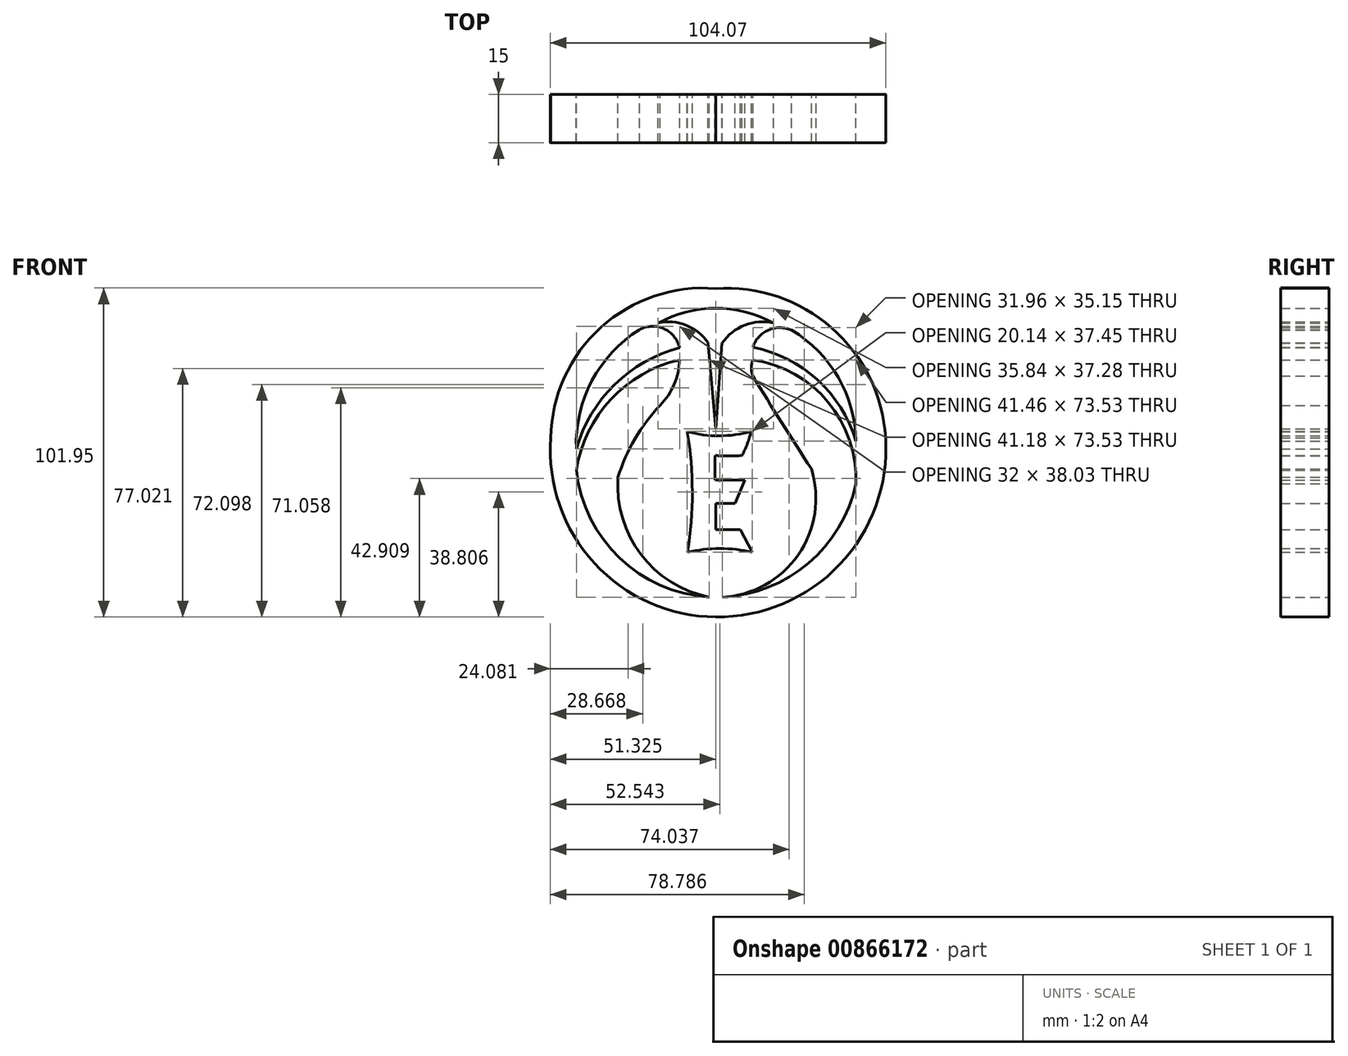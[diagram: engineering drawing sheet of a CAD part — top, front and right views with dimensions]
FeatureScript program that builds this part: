
annotation { "Feature Type Name" : "Feature", "Feature Type Description" : "" }
export const myFeature = defineFeature(function(context is Context, id is Id, definition is map)
    precondition{}
    {
        {
            var Q0;
            Q0=qCreatedBy(makeId("Front.planeOp"),FACE);
            var sketch = newSketch(context, id + "F0", { "sketchPlane" : qUnion([Q0])});
            skArc(sketch, "E0", {"start": v(0, 46.3) * mm, "mid": v(-35.58, 34.22) * mm, "end": v(-51.11, 0) * mm});
            skPoint(sketch, "E0.startSnap0", {"position": v(3.57, 46.3) * mm});
            skArc(sketch, "E1", {"start": v(-51.11, 0) * mm, "mid": v(-37.6, -38.84) * mm, "end": v(0, -55.5) * mm});
            skArc(sketch, "E2", {"start": v(0, -55.5) * mm, "mid": v(38.46, -39.25) * mm, "end": v(52.7, 0) * mm});
            skArc(sketch, "E3", {"start": v(52.7, 0) * mm, "mid": v(35.98, 34.1) * mm, "end": v(0, 46.3) * mm});
            skArc(sketch, "E4", {"start": v(-23.6, 33.52) * mm, "mid": v(-38.38, 17.67) * mm, "end": v(-43.18, -3.45) * mm});
            skArc(sketch, "E5", {"start": v(-11.18, 27.93) * mm, "mid": v(-31.35, 16.5) * mm, "end": v(-43.18, -3.45) * mm});
            skArc(sketch, "E6", {"start": v(-11.18, 27.93) * mm, "mid": v(-16, 33.83) * mm, "end": v(-23.6, 33.52) * mm});
            skArc(sketch, "E7", {"start": v(-11.18, 24.17) * mm, "mid": v(-32.46, 12) * mm, "end": v(-43.18, -10.06) * mm});
            skArc(sketch, "E8", {"start": v(-43.18, -10.06) * mm, "mid": v(-29.76, -37.21) * mm, "end": v(-2, -49.35) * mm});
            skArc(sketch, "E9", {"start": v(-30.26, -12.15) * mm, "mid": v(-23.15, -36.08) * mm, "end": v(-2, -49.35) * mm});
            skArc(sketch, "E10", {"start": v(-17.2, 10.07) * mm, "mid": v(-25, -0.3) * mm, "end": v(-30.26, -12.15) * mm});
            skArc(sketch, "E11", {"start": v(-17.2, 10.07) * mm, "mid": v(-12.89, 16.56) * mm, "end": v(-11.18, 24.17) * mm});
            skArc(sketch, "E12", {"start": v(43.5, -0.98) * mm, "mid": v(31.57, 18) * mm, "end": v(11.54, 28.12) * mm});
            skArc(sketch, "E13", {"start": v(43.5, -0.98) * mm, "mid": v(38, 18.8) * mm, "end": v(23.55, 33.39) * mm});
            skArc(sketch, "E14", {"start": v(23.55, 33.39) * mm, "mid": v(16.37, 33.43) * mm, "end": v(11.54, 28.12) * mm});
            skArc(sketch, "E15", {"start": v(43.5, -14.26) * mm, "mid": v(34.9, 11.09) * mm, "end": v(11.54, 24.17) * mm});
            skArc(sketch, "E16", {"start": v(2.05, -49.35) * mm, "mid": v(28.73, -38.84) * mm, "end": v(43.5, -14.26) * mm});
            skArc(sketch, "E17", {"start": v(2.05, -49.35) * mm, "mid": v(25.61, -36.24) * mm, "end": v(29.71, -9.58) * mm});
            skArc(sketch, "E18", {"start": v(11.54, 19.16) * mm, "mid": v(20.5, 4.72) * mm, "end": v(29.71, -9.58) * mm});
            skArc(sketch, "E19", {"start": v(11.54, 24.17) * mm, "mid": v(11.04, 21.67) * mm, "end": v(11.54, 19.16) * mm});
            skArc(sketch, "E20", {"start": v(-8.79, 1.94) * mm, "mid": v(1.13, 0.63) * mm, "end": v(11.04, 2.03) * mm});
            skPoint(sketch, "E20.endSnap0", {"position": v(11.04, 21.67) * mm});
            skArc(sketch, "E21", {"start": v(8.21, -5.45) * mm, "mid": v(9.83, -1.79) * mm, "end": v(11.04, 2.03) * mm});
            skArc(sketch, "E22", {"start": v(-0.1, -5.45) * mm, "mid": v(4.05, -5.58) * mm, "end": v(8.21, -5.45) * mm});
            skArc(sketch, "E23", {"start": v(-0.1, -5.45) * mm, "mid": v(-0.26, -9.29) * mm, "end": v(-0.1, -13.12) * mm});
            skLineSegment(sketch, "E24", {"start": v(-0.1, -13.12) * mm, "end": v(9.06, -13.12) * mm});
            skLineSegment(sketch, "E25", {"start": v(9.06, -13.12) * mm, "end": v(6, -20.26) * mm});
            skLineSegment(sketch, "E26", {"start": v(6, -20.26) * mm, "end": v(0, -20.26) * mm});
            skLineSegment(sketch, "E27", {"start": v(0, -20.26) * mm, "end": v(0, -28.36) * mm});
            skLineSegment(sketch, "E28", {"start": v(0, -28.36) * mm, "end": v(7.63, -28.36) * mm});
            skLineSegment(sketch, "E29", {"start": v(7.63, -28.36) * mm, "end": v(11.35, -35.42) * mm});
            skArc(sketch, "E30", {"start": v(11.35, -35.42) * mm, "mid": v(1.33, -34.29) * mm, "end": v(-8.7, -35.42) * mm});
            skArc(sketch, "E31", {"start": v(-8.7, -35.42) * mm, "mid": v(-7.24, -16.74) * mm, "end": v(-8.79, 1.94) * mm});
            skLineSegment(sketch, "E32", {"start": v(-2.34, 29.5) * mm, "end": v(0, 2.88) * mm});
            skLineSegment(sketch, "E33", {"start": v(0, 2.88) * mm, "end": v(2, 29.34) * mm});
            skArc(sketch, "E34", {"start": v(17.99, 35.58) * mm, "mid": v(9.03, 34.95) * mm, "end": v(2, 29.34) * mm});
            skArc(sketch, "E35", {"start": v(17.99, 35.58) * mm, "mid": v(0.06, 40.16) * mm, "end": v(-17.86, 35.58) * mm});
            skArc(sketch, "E36", {"start": v(-2.34, 29.5) * mm, "mid": v(-9.16, 34.93) * mm, "end": v(-17.86, 35.58) * mm});
            skSolve(sketch);
        }
        {
            var Q0;
            Q0 = qSketchRegion(id + "F0", true);
            extrude(context, id + "F1", {"entities" : qUnion([Q0]), "depth" : 15 * mm, "offsetDistance" : 25.4 * mm});
        }
    });
